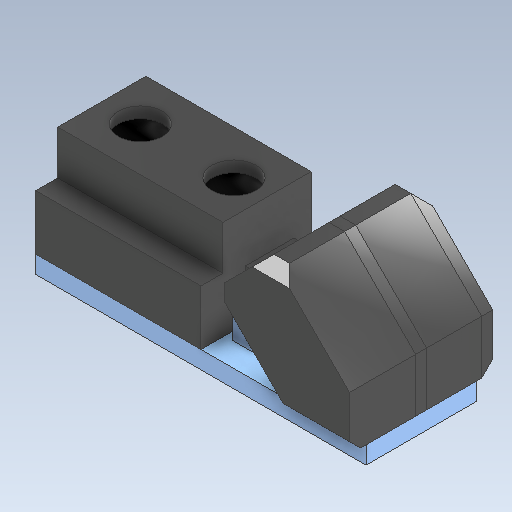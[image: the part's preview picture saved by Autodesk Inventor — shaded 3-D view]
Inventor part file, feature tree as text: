
AUTODESK INVENTOR PART (.ipt)
format: ipt  version: 2020 (Build 240168000, 168)  size: 276,480 bytes
history: native  units: in
note: dims shown in document units (in); Inventor stores cm internally (conversion verified against a paired STEP export)
features: sketch x11, other x7, plane x4
ambient origin geometry x8: Origin, YZ Plane, XZ Plane, XY Plane, X Axis, Y Axis, Z Axis, Center Point
bodies: Solid1 (feature_tree), Solid2 (feature_tree), Solid3 (feature_tree), Solid4 (feature_tree), Solid5 (feature_tree)
feature tree (22):
  other  "Sharp_Czujnik_Linia.ipt"
  other  "Bryła1::Sharp_Czujnik_Linia.ipt"
  other  "Solid2::Sharp_Czujnik_Linia.ipt"
  other  "Solid3::Sharp_Czujnik_Linia.ipt"
  other  "Solid4::Sharp_Czujnik_Linia.ipt"
  other  "Solid6::Sharp_Czujnik_Linia.ipt"
  other  "TaggingFeature1"
  sketch  "Szkic1"
  sketch  "Szkic2"
  sketch  "Szkic3"
  sketch  "Sketch4"  dims[d0=0.3937in]
  sketch  "Sketch5"
  sketch  "Sketch7"
  sketch  "Sketch9"
  sketch  "Sketch8"
  sketch  "Sketch10"
  sketch  "Sketch12"
  sketch  "Sketch13"
  plane  "Work Plane1"
  plane  "Work Plane2"
  plane  "Work Plane3"
  plane  "Work Plane4"
